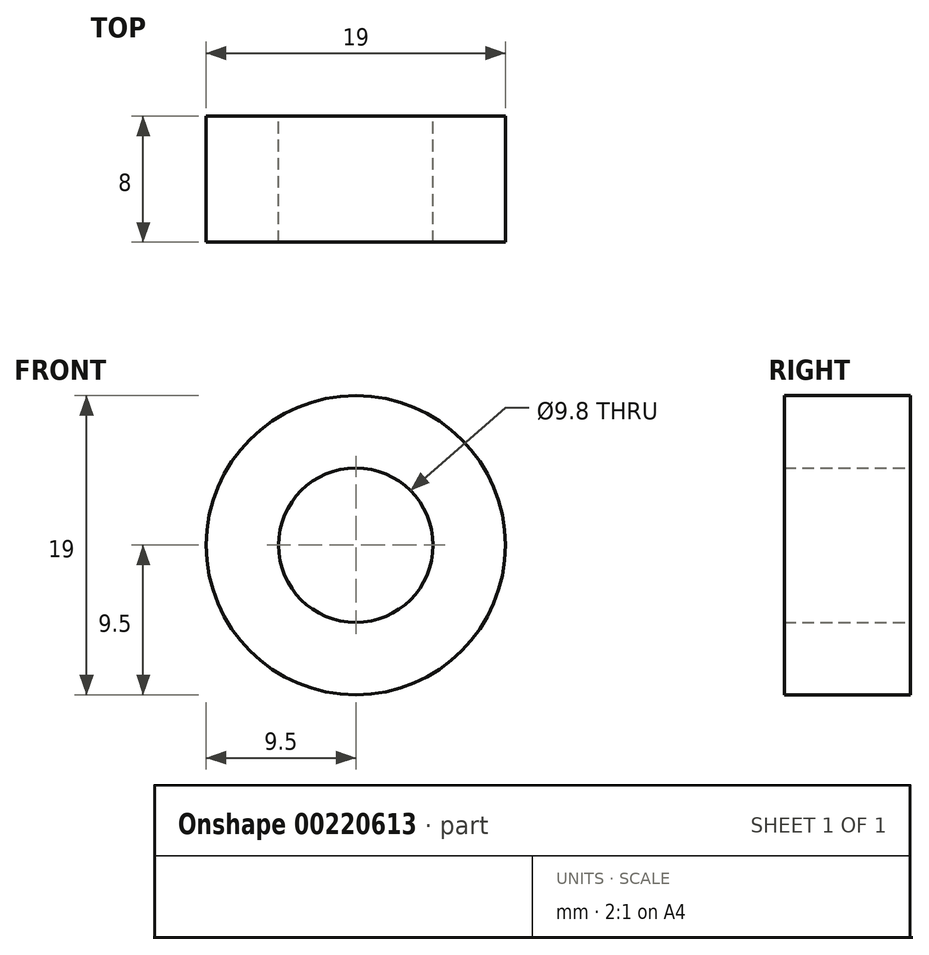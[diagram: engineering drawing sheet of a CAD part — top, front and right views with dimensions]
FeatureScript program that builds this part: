
annotation { "Feature Type Name" : "Feature", "Feature Type Description" : "" }
export const myFeature = defineFeature(function(context is Context, id is Id, definition is map)
    precondition{}
    {
        {
            var Q0;
            Q0=qCreatedBy(makeId("Front.planeOp"),FACE);
            var sketch = newSketch(context, id + "F0", { "sketchPlane" : qUnion([Q0])});
            skCircle(sketch, "E0", {"center": v(0, 0) * mm, "radius": 9.5 * mm});
            skCircle(sketch, "E1", {"center": v(0, 0) * mm, "radius": 4.9 * mm});
            skSolve(sketch);
        }
        {
            var Q0;
            Q0=makeQuery(id+"F0.imprint","IMPRINT",FACE,{"disambiguationData":[TD([[makeQuery(id+"F0.imprint","IMPRINT",EDGE,{"derivedFrom":sQuery(id+"F0.wireOp",EDGE,"E0")}),1.0]])]});
            extrude(context, id + "F1", {"entities" : qUnion([Q0]), "depth" : 8 * mm});
        }
    });
